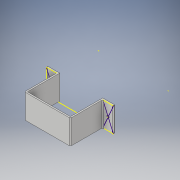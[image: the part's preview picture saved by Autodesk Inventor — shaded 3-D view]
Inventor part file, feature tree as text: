
AUTODESK INVENTOR PART (.ipt)
format: ipt  version: 2019 (Build 230136000, 136)  size: 219,648 bytes
history: native  units: mm
features: sketch x4, other x4, hole x4, move_body x2, extrude x1, direct_edit x1, split x1, chamfer x1
ambient origin geometry x8: Origin, YZ Plane, XZ Plane, XY Plane, X Axis, Y Axis, Z Axis, Center Point
bodies: Solid1 (feature_tree), Solid2 (feature_tree), Solid3 (feature_tree)
feature tree (18):
  extrude  "Extrusion1"  Depth=53.4mm
  direct_edit  "Direct Edit1"
  split  "Split1"
  sketch  "Sketch3"  dims[d4=17.5mm d5=53.4mm]
  sketch  "Sketch4"  dims[d6=75.936mm d7=53.4mm d8=17.5mm d9=20.0mm d10=53.4mm d11=92.4mm d12=20.0mm d13=2.5mm d14=15.0mm d15=0.0mm d16=0.0mm d17=0.0mm d18=2.8mm d19=0.0mm d20=0.0mm d21=25.0mm d22=10.0mm d23=10.0mm d24=3.0mm d25=6.0mm d26=4.0mm d27=1.5mm d28=90.0deg d29=8.0mm d30=20.594885mm d31=10.0mm d32=10.0mm d33=3.0mm d34=6.0mm d35=4.0mm d36=1.5mm d37=90.0deg d38=8.0mm d39=20.594885mm d40=10.0mm d41=10.0mm d42=3.0mm d43=6.0mm d44=4.0mm d45=1.5mm d46=90.0deg d47=8.0mm d48=20.594885mm d49=10.0mm d50=10.0mm d51=3.0mm d52=6.0mm d53=4.0mm d54=1.5mm d55=90.0deg d56=8.0mm d57=20.594885mm d58=2.0mm d59=2.0mm d60=45.0deg]
  other  "Work Point1"
  other  "Work Point2"
  hole  "Hole1"  [1 undecoded]
  hole  "Hole2"  [1 undecoded]
  other  "Work Point3"
  other  "Work Point4"
  hole  "Hole3"  [1 undecoded]
  hole  "Hole4"  [1 undecoded]
  chamfer  "Chamfer1"  Distance=20.0mm
  sketch  "Sketch1"  dims[d0=20.0mm d1=53.4mm]
  sketch  "Sketch2"  dims[d2=68.4mm d3=2.5mm]
  move_body  "Move1"
  move_body  "Move2"
note: 4 required parameter values undecoded (feature->parameter linkage not recoverable at this tier; creation-order binding heuristic only, values carry confidence <= 0.55)
